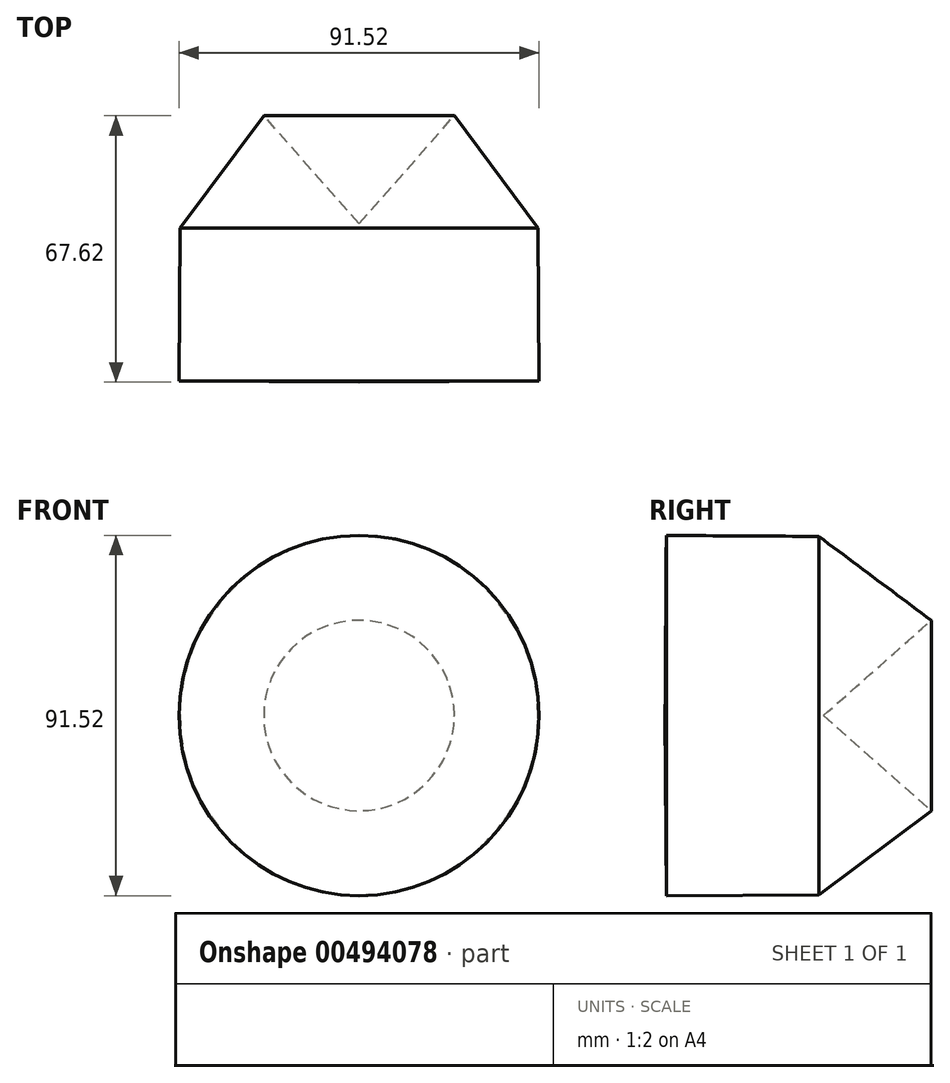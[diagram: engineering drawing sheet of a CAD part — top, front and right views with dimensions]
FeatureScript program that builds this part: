
annotation { "Feature Type Name" : "Feature", "Feature Type Description" : "" }
export const myFeature = defineFeature(function(context is Context, id is Id, definition is map)
    precondition{}
    {
        {
            var Q0;
            Q0=qCreatedBy(makeId("Top.planeOp"),FACE);
            var sketch = newSketch(context, id + "F0", { "sketchPlane" : qUnion([Q0])});
            skLineSegment(sketch, "E0", {"start": v(0, 19.1) * mm, "end": v(-24.2, -8.3) * mm});
            skLineSegment(sketch, "E1", {"start": v(-24.2, -8.3) * mm, "end": v(-24.2, -48.53) * mm});
            skLineSegment(sketch, "E2", {"start": v(-24.2, -48.53) * mm, "end": v(21.57, -48.24) * mm});
            skLineSegment(sketch, "E3", {"start": v(21.57, -48.24) * mm, "end": v(21.32, -9.47) * mm});
            skLineSegment(sketch, "E4", {"start": v(21.32, -9.47) * mm, "end": v(0, 19.1) * mm});
            skSolve(sketch);
        }
        {
            var Q0;
            Q0=qCreatedBy(makeId("Top.planeOp"),FACE);
            cPlane(context, id + "F1", {"entities" : qUnion([Q0]), "cplaneType" : CPlaneType.OFFSET, "offset" : 254 * mm, "width" : 152.4 * mm, "height" : 152.4 * mm});
        }
        {
            var Q0;
            Q0=makeQuery(id+"F0.imprint","IMPRINT",FACE,{"disambiguationData":[TD([[makeQuery(id+"F0.imprint","IMPRINT",EDGE,{"derivedFrom":sQuery(id+"F0.wireOp",EDGE,"E0")}),1.0]])]});
            var Q1;
            Q1=sQuery(id+"F0.wireOp",EDGE,"E1");
            revolve(context, id + "F2", {"entities" : qUnion([Q0]), "axis" : qUnion([Q1]), "revolveType" : RevolveType.FULL});
        }
    });
